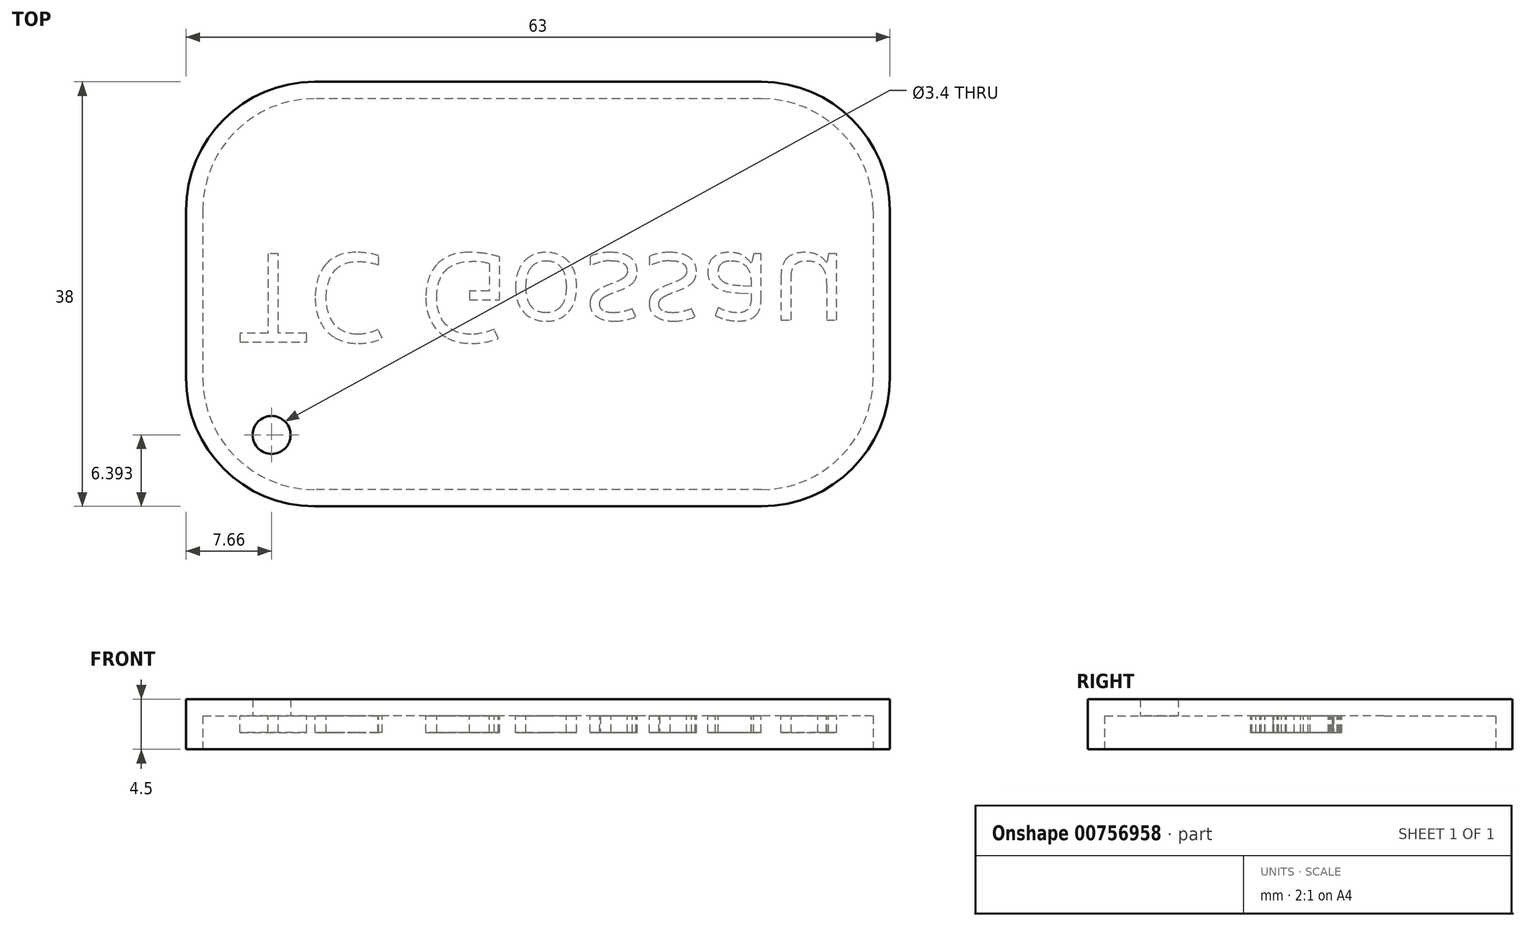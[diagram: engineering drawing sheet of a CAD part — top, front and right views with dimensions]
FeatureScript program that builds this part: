
annotation { "Feature Type Name" : "Feature", "Feature Type Description" : "" }
export const myFeature = defineFeature(function(context is Context, id is Id, definition is map)
    precondition{}
    {
        {
            var Q0;
            Q0=qCreatedBy(makeId("Top.planeOp"),FACE);
            var sketch = newSketch(context, id + "F0", { "sketchPlane" : qUnion([Q0])});
            skLineSegment(sketch, "E0.bottom", {"start": v(30, 17.5) * mm, "end": v(-30, 17.5) * mm});
            skLineSegment(sketch, "E0.top", {"start": v(30, -17.5) * mm, "end": v(-30, -17.5) * mm});
            skLineSegment(sketch, "E0.left", {"start": v(30, 17.5) * mm, "end": v(30, -17.5) * mm});
            skLineSegment(sketch, "E0.right", {"start": v(-30, 17.5) * mm, "end": v(-30, -17.5) * mm});
            skPoint(sketch, "E0.middle", {"position": v(0, 0) * mm});
            skSolve(sketch);
        }
        {
            var Q0;
            Q0=makeQuery(id+"F0.imprint","IMPRINT",FACE,{"disambiguationData":[TD([[makeQuery(id+"F0.imprint","IMPRINT",EDGE,{"derivedFrom":sQuery(id+"F0.wireOp",EDGE,"E0.bottom")}),1.0]])]});
            extrude(context, id + "F1", {"entities" : qUnion([Q0]), "depth" : 3 * mm, "offsetDistance" : 25 * mm});
        }
        {
            var Q0;
            Q0=makeQuery(id+"F1.opExtrude","SWEPT_EDGE",EDGE,{"disambiguationData":[OSD([sQuery(id+"F0.wireOp",EDGE,"E0.bottom"),sQuery(id+"F0.wireOp",EDGE,"E0.left")])]});
            var Q1;
            Q1=makeQuery(id+"F1.opExtrude","SWEPT_EDGE",EDGE,{"disambiguationData":[OSD([sQuery(id+"F0.wireOp",EDGE,"E0.top"),sQuery(id+"F0.wireOp",EDGE,"E0.right")])]});
            var Q2;
            Q2=makeQuery(id+"F1.opExtrude","SWEPT_EDGE",EDGE,{"disambiguationData":[OSD([sQuery(id+"F0.wireOp",EDGE,"E0.top"),sQuery(id+"F0.wireOp",EDGE,"E0.left")])]});
            var Q3;
            Q3=makeQuery(id+"F1.opExtrude","SWEPT_EDGE",EDGE,{"disambiguationData":[OSD([sQuery(id+"F0.wireOp",EDGE,"E0.bottom"),sQuery(id+"F0.wireOp",EDGE,"E0.right")])]});
            fillet(context, id + "F2", {"entities" : qUnion([Q0, Q1, Q2, Q3]), "radius" : 10 * mm, "tangentPropagation" : true, "allowEdgeOverflow" : false});
        }
        {
            var Q0;
            Q0=makeQuery(id+"F1.opExtrude","CAP_FACE",FACE,{"disambiguationData":[OSD([sQuery(id+"F0.wireOp",EDGE,"E0.bottom"),sQuery(id+"F0.wireOp",EDGE,"E0.top"),sQuery(id+"F0.wireOp",EDGE,"E0.left"),sQuery(id+"F0.wireOp",EDGE,"E0.right")])],"isStart":true});
            shell(context, id + "F3", {"entities" : qUnion([Q0]), "thickness" : 1.5 * mm, "oppositeDirection" : true});
        }
        {
            var Q0;
            Q0=makeQuery(id+"F3.opShell","OFFSET_FACE",FACE,{"disambiguationData":[OSD([sQuery(id+"F0.wireOp",EDGE,"E0.bottom"),sQuery(id+"F0.wireOp",EDGE,"E0.top"),sQuery(id+"F0.wireOp",EDGE,"E0.left"),sQuery(id+"F0.wireOp",EDGE,"E0.right")])]});
            var sketch = newSketch(context, id + "F4", { "sketchPlane" : qUnion([Q0])});
            skText(sketch, "E1", { "text": "TC Gossau", "fontName": "OpenSans-Regular.ttf"});
            const initialGuessF4  = {"E1": [-0.02676, -0.00363, 1, 0, 0.008]};
            skSetInitialGuess(sketch, initialGuessF4);
            skSolve(sketch);
        }
        {
            var Q0;
            Q0 = qSketchRegion(id + "F4", true);
            extrude(context, id + "F5", {"entities" : qUnion([Q0]), "operationType" : NewBodyOperationType.ADD, "depth" : 1.5 * mm, "offsetDistance" : 25 * mm});
        }
        {
            var Q0;
            {var subQ0=sQuery(id+"F0.wireOp",EDGE,"E0.right");var subQ1=sQuery(id+"F0.wireOp",EDGE,"E0.top");var subQ2=sQuery(id+"F0.wireOp",EDGE,"E0.left");var subQ3=sQuery(id+"F0.wireOp",EDGE,"E0.bottom");Q0=makeQuery(id+"F5.boolean.opBoolean","SPLIT",FACE,{"disambiguationData":[TD([makeQuery(id+"F3.opShell","OFFSET_FACE",FACE,{"disambiguationData":[OSD([subQ3])]})])],"derivedFrom":makeQuery(id+"F3.opShell","OFFSET_FACE",FACE,{"disambiguationData":[OSD([subQ3,subQ1,subQ2,subQ0])]})});}
            var sketch = newSketch(context, id + "F6", { "sketchPlane" : qUnion([Q0])});
            skPoint(sketch, "E2", {"position": v(-23.84, 12.6) * mm});
            skSolve(sketch);
        }
        {
            var Q0;
            Q0=sQuery(id+"F6.wireOp",VERTEX,"E2");
            var Q1;
            Q1=makeQuery(id+"F1.opExtrude","SWEPT_BODY",BODY,{"disambiguationData":[OSD([sQuery(id+"F0.wireOp",EDGE,"E0.bottom"),sQuery(id+"F0.wireOp",EDGE,"E0.top"),sQuery(id+"F0.wireOp",EDGE,"E0.left"),sQuery(id+"F0.wireOp",EDGE,"E0.right")])]});
            hole(context, id + "F7", {"style" : HoleStyle.SIMPLE, "endStyle" : HoleEndStyle.THROUGH, "holeDiameter" : 3.4 * mm, "majorDiameter" : 5 * mm, "isTappedThrough" : true, "tappedDepth" : 12 * mm, "tapClearance" : 3, "locations" : qUnion([Q0]), "scope" : qUnion([Q1])});
        }
    });
